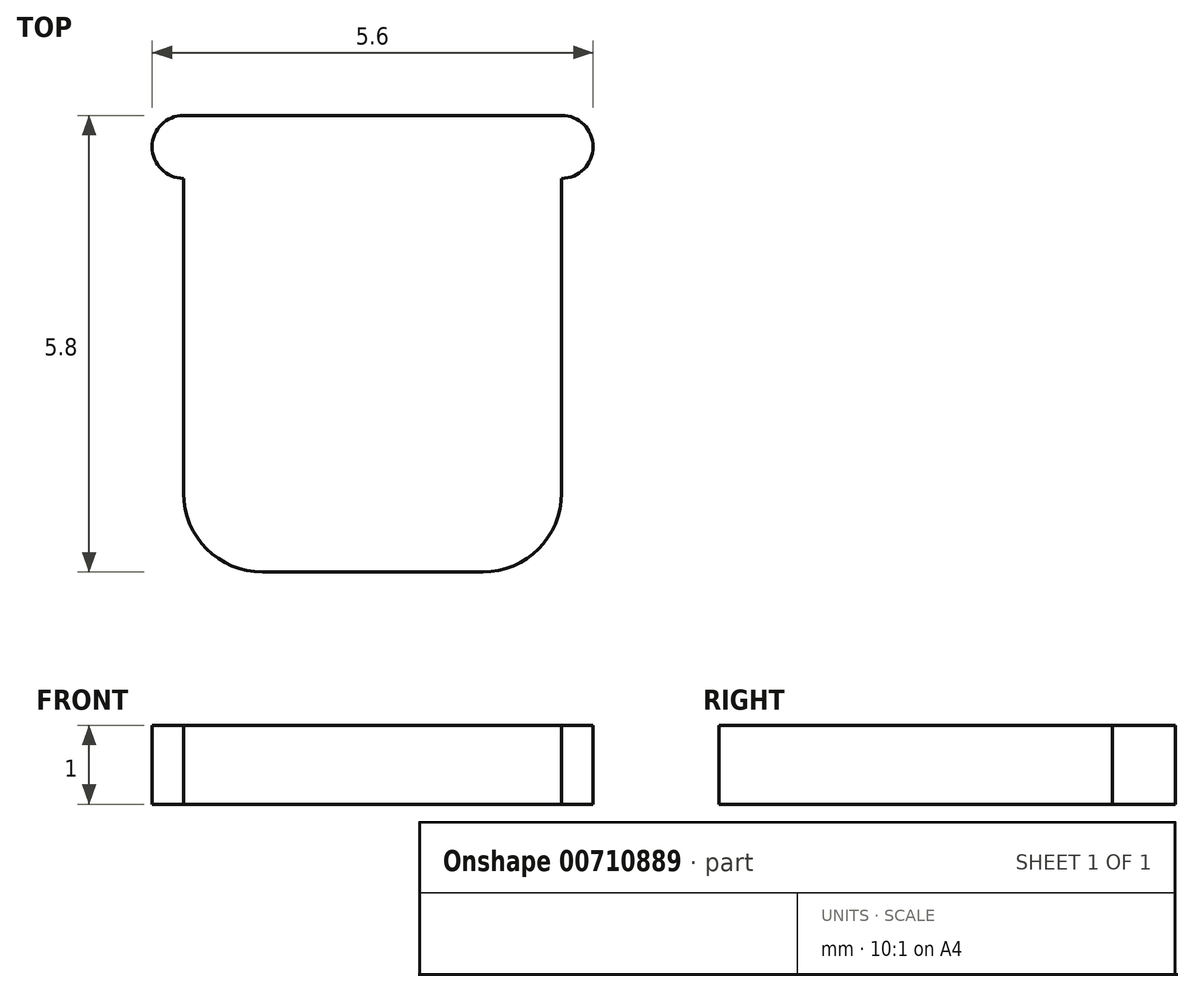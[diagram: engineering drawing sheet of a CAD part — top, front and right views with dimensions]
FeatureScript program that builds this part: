
annotation { "Feature Type Name" : "Feature", "Feature Type Description" : "" }
export const myFeature = defineFeature(function(context is Context, id is Id, definition is map)
    precondition{}
    {
        {
            var Q0;
            Q0=qCreatedBy(makeId("Top.planeOp"),FACE);
            var sketch = newSketch(context, id + "F0", { "sketchPlane" : qUnion([Q0])});
            skLineSegment(sketch, "E0.bottom", {"start": v(2.4, -2.5) * mm, "end": v(-2.4, -2.5) * mm});
            skLineSegment(sketch, "E0.top", {"start": v(2.4, 2.5) * mm, "end": v(-2.4, 2.5) * mm});
            skLineSegment(sketch, "E0.left", {"start": v(2.4, -2.5) * mm, "end": v(2.4, 2.5) * mm});
            skLineSegment(sketch, "E0.right", {"start": v(-2.4, -2.5) * mm, "end": v(-2.4, 2.5) * mm});
            skPoint(sketch, "E0.middle", {"position": v(0, 0) * mm});
            skLineSegment(sketch, "E1", {"start": v(2.4, 3.3) * mm, "end": v(0, 3.3) * mm});
            skPoint(sketch, "E2", {"position": v(2.4, 3.3) * mm});
            skArc(sketch, "E3", {"start": v(2.4, 2.5) * mm, "mid": v(2.8, 2.9) * mm, "end": v(2.4, 3.3) * mm});
            skLineSegment(sketch, "E4", {"start": v(0, 3.3) * mm, "end": v(0, 0) * mm, "construction": true});
            skArc(sketch, "E5.MirrorCS", {"start": v(-2.4, 2.5) * mm, "mid": v(-2.8, 2.9) * mm, "end": v(-2.4, 3.3) * mm});
            skLineSegment(sketch, "E6.MirrorCS", {"start": v(-2.4, 3.3) * mm, "end": v(0, 3.3) * mm});
            skSolve(sketch);
        }
        {
            var Q0;
            Q0=makeQuery(id+"F0.imprint","IMPRINT",FACE,{"disambiguationData":[TD([[makeQuery(id+"F0.imprint","IMPRINT",EDGE,{"derivedFrom":sQuery(id+"F0.wireOp",EDGE,"E0.top")}),-1.0]])]});
            var Q1;
            Q1=makeQuery(id+"F0.imprint","IMPRINT",FACE,{"disambiguationData":[TD([[makeQuery(id+"F0.imprint","IMPRINT",EDGE,{"derivedFrom":sQuery(id+"F0.wireOp",EDGE,"E0.bottom")}),-1.0]])]});
            extrude(context, id + "F1", {"entities" : qUnion([Q0, Q1]), "depth" : 1 * mm, "offsetDistance" : 25 * mm});
        }
        {
            var Q0;
            Q0=makeQuery(id+"F1.opExtrude","SWEPT_EDGE",EDGE,{"disambiguationData":[OSD([sQuery(id+"F0.wireOp",EDGE,"E0.bottom"),sQuery(id+"F0.wireOp",EDGE,"E0.right")])]});
            var Q1;
            Q1=makeQuery(id+"F1.opExtrude","SWEPT_EDGE",EDGE,{"disambiguationData":[OSD([sQuery(id+"F0.wireOp",EDGE,"E0.bottom"),sQuery(id+"F0.wireOp",EDGE,"E0.left")])]});
            fillet(context, id + "F2", {"entities" : qUnion([Q0, Q1]), "radius" : 1 * mm, "tangentPropagation" : true, "allowEdgeOverflow" : false});
        }
    });
